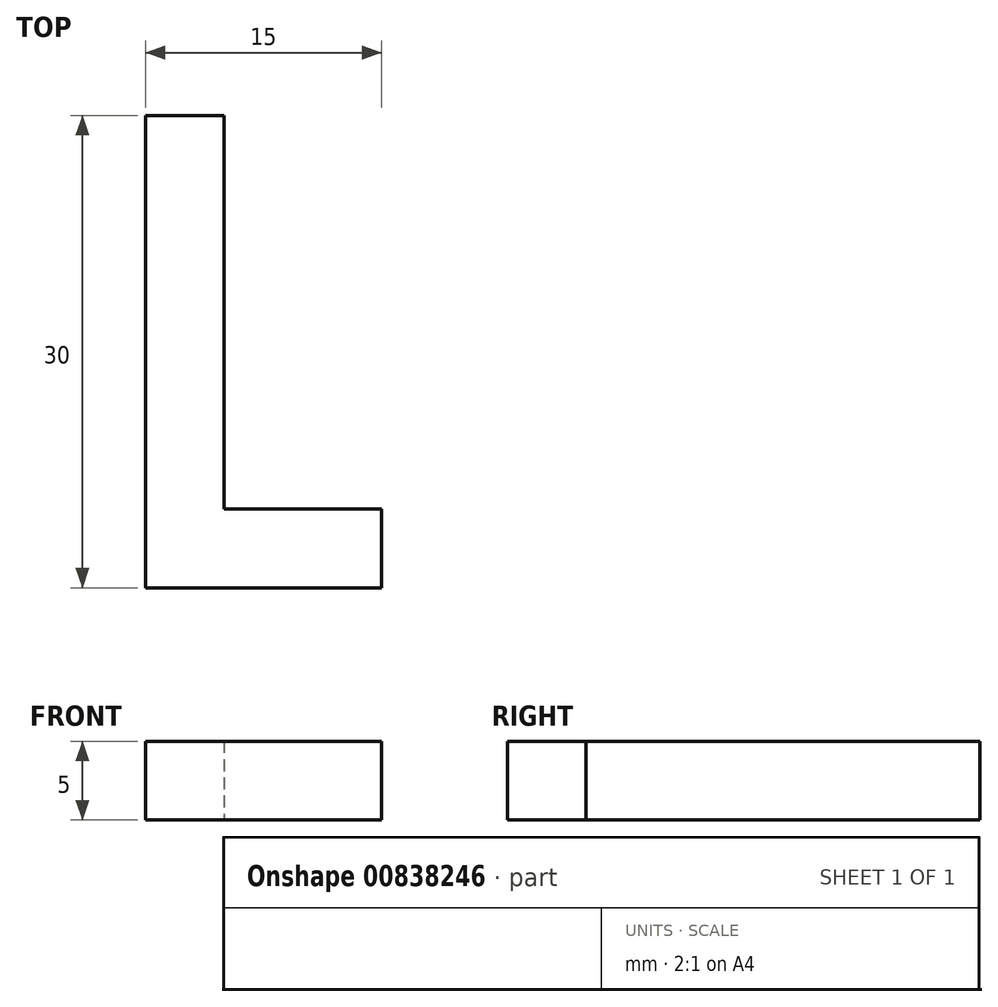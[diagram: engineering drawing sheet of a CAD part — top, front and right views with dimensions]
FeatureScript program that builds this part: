
annotation { "Feature Type Name" : "Feature", "Feature Type Description" : "" }
export const myFeature = defineFeature(function(context is Context, id is Id, definition is map)
    precondition{}
    {
        {
            var Q0;
            Q0=qCreatedBy(makeId("Top.planeOp"),FACE);
            var sketch = newSketch(context, id + "F0", { "sketchPlane" : qUnion([Q0])});
            skLineSegment(sketch, "E0", {"start": v(-9.9, 30) * mm, "end": v(-9.9, 0) * mm});
            skLineSegment(sketch, "E1", {"start": v(-9.9, 0) * mm, "end": v(5.1, 0) * mm});
            skLineSegment(sketch, "E2", {"start": v(5.1, 0) * mm, "end": v(5.1, 5) * mm});
            skLineSegment(sketch, "E3", {"start": v(5.1, 5) * mm, "end": v(-4.9, 5) * mm});
            skLineSegment(sketch, "E4", {"start": v(-4.9, 5) * mm, "end": v(-4.9, 30) * mm});
            skLineSegment(sketch, "E5", {"start": v(-4.9, 30) * mm, "end": v(-9.9, 30) * mm});
            skSolve(sketch);
        }
        {
            var Q0;
            Q0 = qSketchRegion(id + "F0", true);
            extrude(context, id + "F1", {"entities" : qUnion([Q0]), "depth" : 5 * mm, "offsetDistance" : 25 * mm});
        }
    });
